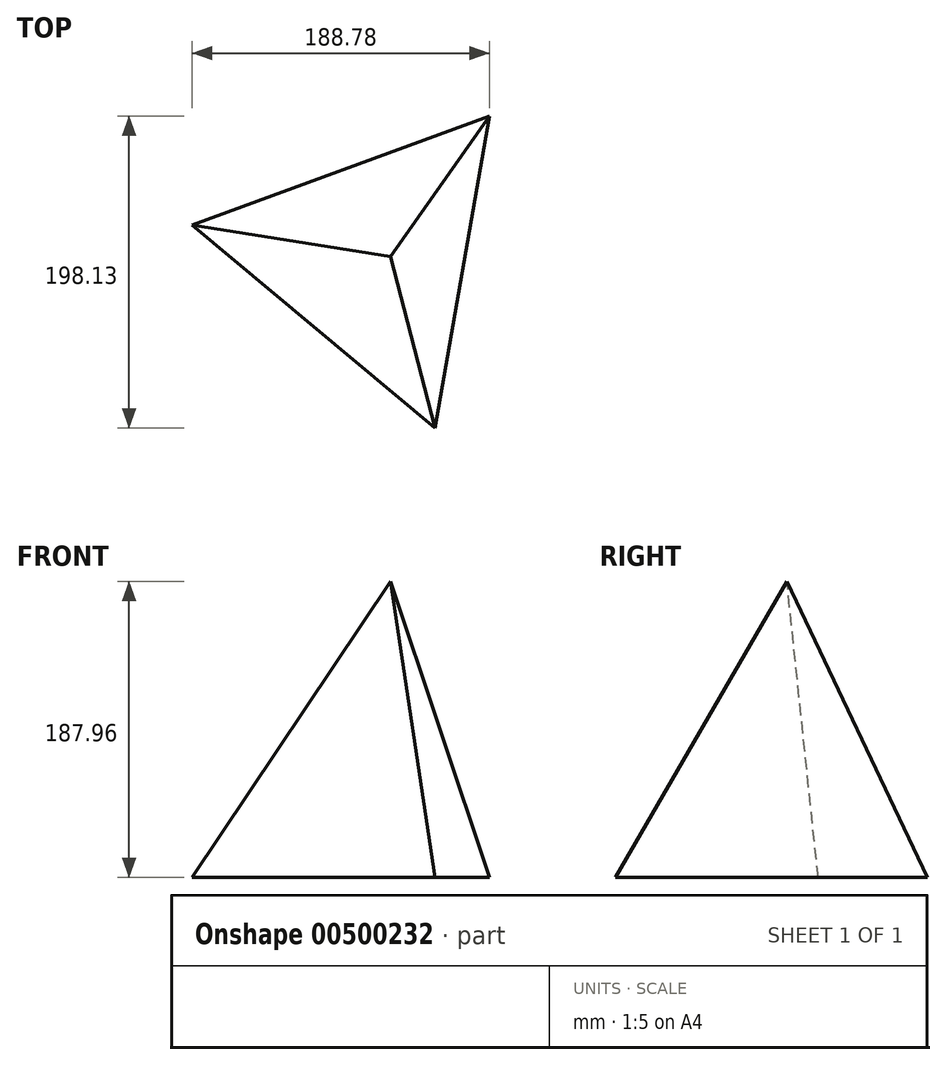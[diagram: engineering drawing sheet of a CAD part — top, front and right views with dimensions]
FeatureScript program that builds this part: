
annotation { "Feature Type Name" : "Feature", "Feature Type Description" : "" }
export const myFeature = defineFeature(function(context is Context, id is Id, definition is map)
    precondition{}
    {
        {
            var Q0;
            Q0=qCreatedBy(makeId("Top.planeOp"),FACE);
            var sketch = newSketch(context, id + "F0", { "sketchPlane" : qUnion([Q0])});
            skCircle(sketch, "E0.cCircle", {"center": v(0, 0) * mm, "radius": 116.1 * mm, "construction": true});
            skLineSegment(sketch, "E0.0", {"start": v(74.4, 89.14) * mm, "end": v(40, -109) * mm});
            skLineSegment(sketch, "E0.1", {"start": v(40, -109) * mm, "end": v(-114.4, 19.86) * mm});
            skLineSegment(sketch, "E0.2", {"start": v(-114.4, 19.86) * mm, "end": v(74.4, 89.14) * mm});
            skSolve(sketch);
        }
        {
            var Q0;
            Q0=qCreatedBy(makeId("Top.planeOp"),FACE);
            cPlane(context, id + "F1", {"entities" : qUnion([Q0]), "cplaneType" : CPlaneType.OFFSET, "offset" : 187.96 * mm, "width" : 152.4 * mm, "height" : 152.4 * mm});
        }
        {
            var Q0;
            Q0=qCreatedBy(id+"F1.planeOp",FACE);
            var sketch = newSketch(context, id + "F2", { "sketchPlane" : qUnion([Q0])});
            skPoint(sketch, "E1", {"position": v(11.58, 0) * mm});
            skSolve(sketch);
        }
        {
            var Q0;
            Q0=makeQuery(id+"F0.imprint","IMPRINT",FACE,{"disambiguationData":[TD([[makeQuery(id+"F0.imprint","IMPRINT",EDGE,{"derivedFrom":sQuery(id+"F0.wireOp",EDGE,"E0.0")}),-1.0]])]});
            var Q1;
            Q1=sQuery(id+"F2.wireOp",VERTEX,"E1");
            loft(context, id + "F3", {"sheetProfilesArray" : [{ "sheetProfileEntities" : qUnion([Q0]) }, { "sheetProfileEntities" : qUnion([Q1]) }]});
        }
    });
